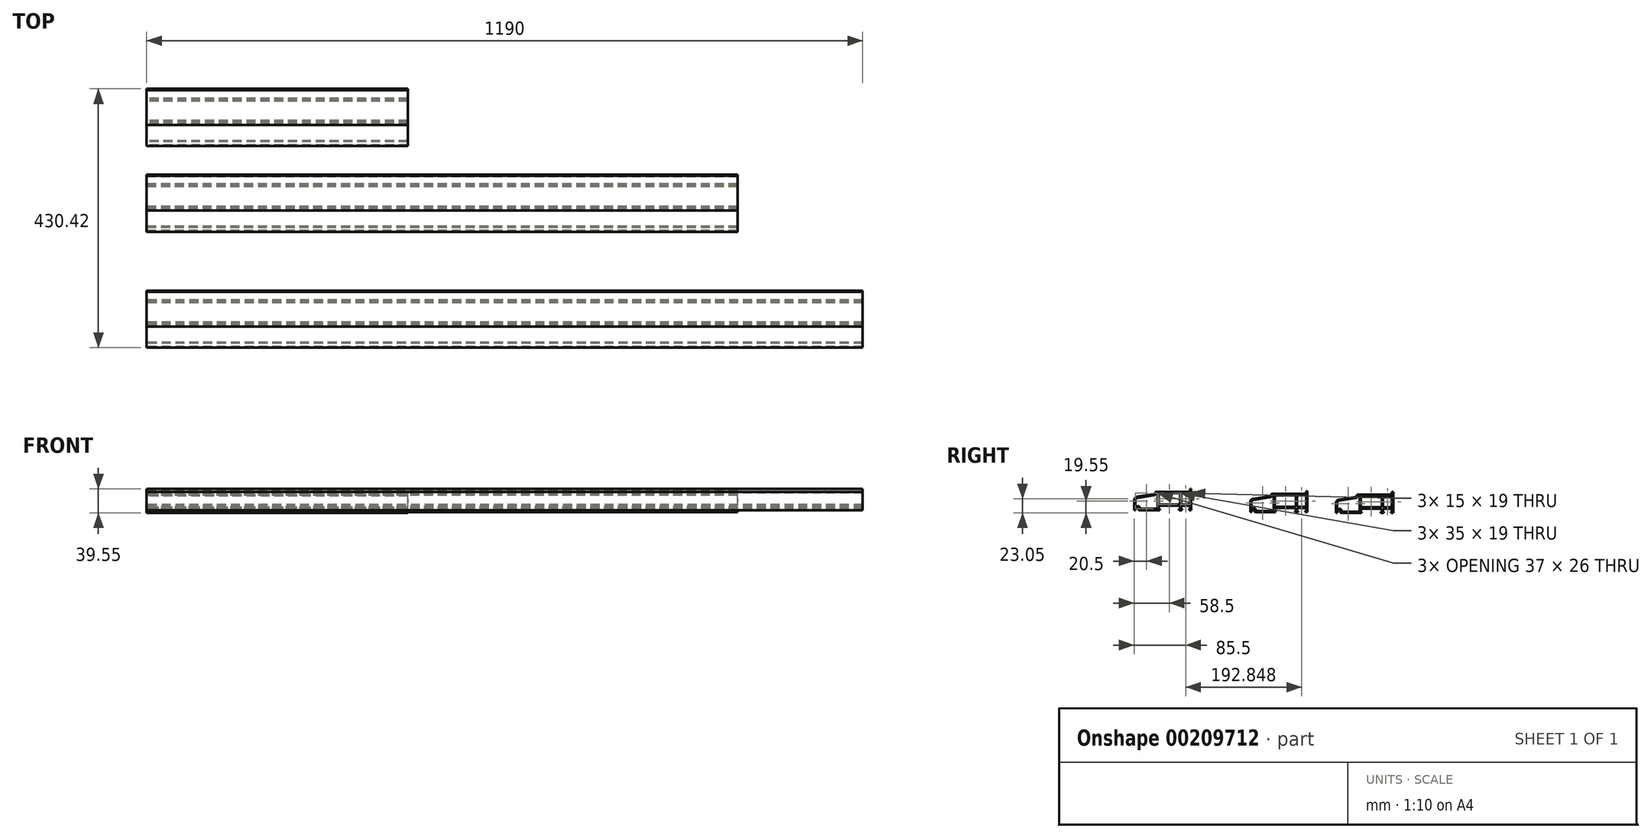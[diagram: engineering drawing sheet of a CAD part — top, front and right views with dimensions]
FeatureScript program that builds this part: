
annotation { "Feature Type Name" : "Feature", "Feature Type Description" : "" }
export const myFeature = defineFeature(function(context is Context, id is Id, definition is map)
    precondition{}
    {
        {
            var Q0;
            Q0=qCreatedBy(makeId("Right.planeOp"),FACE);
            var sketch = newSketch(context, id + "F0", { "sketchPlane" : qUnion([Q0])});
            skLineSegment(sketch, "E0.bottom", {"start": v(0, 0) * mm, "end": v(-3.5, 0) * mm});
            skLineSegment(sketch, "E0.top", {"start": v(-2, 30) * mm, "end": v(-60, 30) * mm});
            skLineSegment(sketch, "E0.left", {"start": v(0, 0) * mm, "end": v(0, 35) * mm});
            skLineSegment(sketch, "E0.right", {"start": v(-95, 0) * mm, "end": v(-95, 16) * mm});
            skArc(sketch, "E1", {"start": v(-89.6, 22.28) * mm, "mid": v(-93.47, 20.14) * mm, "end": v(-95, 16) * mm});
            skLineSegment(sketch, "E2", {"start": v(-89.6, 22.28) * mm, "end": v(-62.97, 26.33) * mm});
            skArc(sketch, "E3", {"start": v(-62.97, 26.33) * mm, "mid": v(-60.77, 27.59) * mm, "end": v(-60, 30) * mm});
            skLineSegment(sketch, "E4.0", {"start": v(-2, 2) * mm, "end": v(-2, 7) * mm});
            skArc(sketch, "E4.1", {"start": v(-62.67, 24.35) * mm, "mid": v(-59.97, 25.56) * mm, "end": v(-58.3, 28) * mm});
            skLineSegment(sketch, "E4.2", {"start": v(-89.3, 20.3) * mm, "end": v(-62.67, 24.35) * mm});
            skLineSegment(sketch, "E4.3", {"start": v(-2, 28) * mm, "end": v(-17, 28) * mm});
            skLineSegment(sketch, "E4.4", {"start": v(-93, 0) * mm, "end": v(-93, 4) * mm});
            skLineSegment(sketch, "E4.5", {"start": v(-2, 2) * mm, "end": v(-3.5, 2) * mm});
            skArc(sketch, "E5.0", {"start": v(-89.3, 20.3) * mm, "mid": v(-91.95, 18.83) * mm, "end": v(-93, 16) * mm});
            skLineSegment(sketch, "E6", {"start": v(-2, 35) * mm, "end": v(0, 35) * mm});
            skLineSegment(sketch, "E7.trimOffspring", {"start": v(-2, 30) * mm, "end": v(-2, 35) * mm});
            skLineSegment(sketch, "E8.0", {"start": v(-17, 2) * mm, "end": v(-17, 7) * mm});
            skLineSegment(sketch, "E9.0", {"start": v(-19, 2) * mm, "end": v(-19, 7) * mm});
            skLineSegment(sketch, "E10.0", {"start": v(-54, 2) * mm, "end": v(-54, 7) * mm});
            skLineSegment(sketch, "E11.0", {"start": v(-56, 2) * mm, "end": v(-56, 28) * mm});
            skLineSegment(sketch, "E12.trimOffspring", {"start": v(-19, 28) * mm, "end": v(-54, 28) * mm});
            skLineSegment(sketch, "E13.trimOffspring", {"start": v(-19, 2) * mm, "end": v(-20.5, 2) * mm});
            skLineSegment(sketch, "E14.trimOffspring", {"start": v(-56, 28) * mm, "end": v(-58.3, 28) * mm});
            skLineSegment(sketch, "E15.trimOffspring", {"start": v(-56, 2) * mm, "end": v(-86, 2) * mm});
            skLineSegment(sketch, "E16.0", {"start": v(-2, 9) * mm, "end": v(-17, 9) * mm});
            skLineSegment(sketch, "E17.0", {"start": v(-2, 7) * mm, "end": v(-17, 7) * mm});
            skLineSegment(sketch, "E18", {"start": v(-52.5, 2) * mm, "end": v(-52.5, 0) * mm});
            skLineSegment(sketch, "E19.trimOffspring", {"start": v(-54, 9) * mm, "end": v(-54, 28) * mm});
            skLineSegment(sketch, "E20", {"start": v(-20.5, 2) * mm, "end": v(-20.5, 0) * mm});
            skLineSegment(sketch, "E21", {"start": v(-15.5, 2) * mm, "end": v(-15.5, 0) * mm});
            skLineSegment(sketch, "E22", {"start": v(-3.5, 2) * mm, "end": v(-3.5, 0) * mm});
            skPoint(sketch, "E23.orphan", {"position": v(-3.5, -2.3) * mm});
            skLineSegment(sketch, "E24.trimOffspring", {"start": v(-15.5, 0) * mm, "end": v(-20.5, 0) * mm});
            skLineSegment(sketch, "E25.trimOffspring", {"start": v(-15.5, 2) * mm, "end": v(-17, 2) * mm});
            skPoint(sketch, "E26.orphan", {"position": v(-15.5, -2.3) * mm});
            skLineSegment(sketch, "E27.trimOffspring", {"start": v(-2, 9) * mm, "end": v(-2, 28) * mm});
            skLineSegment(sketch, "E28.trimOffspring", {"start": v(-17, 9) * mm, "end": v(-17, 28) * mm});
            skLineSegment(sketch, "E29.trimOffspring", {"start": v(-19, 9) * mm, "end": v(-54, 9) * mm});
            skLineSegment(sketch, "E30.trimOffspring", {"start": v(-19, 7) * mm, "end": v(-54, 7) * mm});
            skLineSegment(sketch, "E31.trimOffspring", {"start": v(-19, 9) * mm, "end": v(-19, 28) * mm});
            skPoint(sketch, "E32.orphan", {"position": v(-20.5, -2.3) * mm});
            skLineSegment(sketch, "E33.trimOffspring", {"start": v(-52.5, 2) * mm, "end": v(-54, 2) * mm});
            skLineSegment(sketch, "E34.trimOffspring", {"start": v(-52.5, 0) * mm, "end": v(-86.5, 0) * mm});
            skLineSegment(sketch, "E35", {"start": v(-93, 4) * mm, "end": v(-88.56, 4.57) * mm});
            skLineSegment(sketch, "E36", {"start": v(-88, 4.07) * mm, "end": v(-88, 1.5) * mm});
            skPoint(sketch, "E37.visualSharp", {"position": v(-88, 4.64) * mm});
            skArc(sketch, "E37.filletArc", {"start": v(-88, 4.07) * mm, "mid": v(-88.17, 4.45) * mm, "end": v(-88.56, 4.57) * mm});
            skArc(sketch, "E38.filletArc", {"start": v(-88, 1.5) * mm, "mid": v(-87.56, 0.44) * mm, "end": v(-86.5, 0) * mm});
            skLineSegment(sketch, "E39.0", {"start": v(-86, 4.07) * mm, "end": v(-86, 2) * mm});
            skArc(sketch, "E39.1", {"start": v(-86, 4.07) * mm, "mid": v(-86.85, 5.95) * mm, "end": v(-88.82, 6.55) * mm});
            skLineSegment(sketch, "E39.2", {"start": v(-93, 6.02) * mm, "end": v(-88.82, 6.55) * mm});
            skPoint(sketch, "E40.trimOffspring.end.orphan", {"position": v(-93, 2) * mm});
            skLineSegment(sketch, "E41.trimOffspring", {"start": v(-93, 6.02) * mm, "end": v(-93, 16) * mm});
            skLineSegment(sketch, "E42", {"start": v(-95, 0) * mm, "end": v(-93, 0) * mm});
            skSolve(sketch);
        }
        {
            var Q0;
            Q0 = qSketchRegion(id + "F0", true);
            extrude(context, id + "F1", {"entities" : qUnion([Q0]), "depth" : 1190 * mm, "offsetDistance" : 25 * mm});
        }
        {
            var Q0;
            Q0=qCreatedBy(makeId("Right.planeOp"),FACE);
            var sketch = newSketch(context, id + "F2", { "sketchPlane" : qUnion([Q0])});
            skLineSegment(sketch, "E43.bottom", {"start": v(192.85, -3.3) * mm, "end": v(189.35, -3.3) * mm});
            skLineSegment(sketch, "E43.top", {"start": v(190.85, 26.7) * mm, "end": v(132.85, 26.7) * mm});
            skLineSegment(sketch, "E43.left", {"start": v(192.85, -3.3) * mm, "end": v(192.85, 31.7) * mm});
            skLineSegment(sketch, "E43.right", {"start": v(97.85, -3.3) * mm, "end": v(97.85, 12.7) * mm});
            skArc(sketch, "E44", {"start": v(103.24, 18.98) * mm, "mid": v(99.38, 16.84) * mm, "end": v(97.85, 12.7) * mm});
            skLineSegment(sketch, "E45", {"start": v(103.24, 18.98) * mm, "end": v(129.87, 23.03) * mm});
            skArc(sketch, "E46", {"start": v(129.87, 23.03) * mm, "mid": v(132.07, 24.3) * mm, "end": v(132.85, 26.7) * mm});
            skLineSegment(sketch, "E47.0", {"start": v(190.85, -1.3) * mm, "end": v(190.85, 3.7) * mm});
            skArc(sketch, "E47.1", {"start": v(130.18, 21.05) * mm, "mid": v(132.87, 22.27) * mm, "end": v(134.55, 24.7) * mm});
            skLineSegment(sketch, "E47.2", {"start": v(103.54, 17) * mm, "end": v(130.18, 21.05) * mm});
            skLineSegment(sketch, "E47.3", {"start": v(190.85, 24.7) * mm, "end": v(175.85, 24.7) * mm});
            skLineSegment(sketch, "E47.4", {"start": v(99.85, -3.3) * mm, "end": v(99.85, 0.7) * mm});
            skLineSegment(sketch, "E47.5", {"start": v(190.85, -1.3) * mm, "end": v(189.35, -1.3) * mm});
            skArc(sketch, "E48.0", {"start": v(103.54, 17) * mm, "mid": v(100.9, 15.54) * mm, "end": v(99.85, 12.7) * mm});
            skLineSegment(sketch, "E49", {"start": v(190.85, 31.7) * mm, "end": v(192.85, 31.7) * mm});
            skLineSegment(sketch, "E50.trimOffspring", {"start": v(190.85, 26.7) * mm, "end": v(190.85, 31.7) * mm});
            skLineSegment(sketch, "E51.0", {"start": v(175.85, -1.3) * mm, "end": v(175.85, 3.7) * mm});
            skLineSegment(sketch, "E52.0", {"start": v(173.85, -1.3) * mm, "end": v(173.85, 3.7) * mm});
            skLineSegment(sketch, "E53.0", {"start": v(138.85, -1.3) * mm, "end": v(138.85, 3.7) * mm});
            skLineSegment(sketch, "E54.0", {"start": v(136.85, -1.3) * mm, "end": v(136.85, 24.7) * mm});
            skLineSegment(sketch, "E55.trimOffspring", {"start": v(173.85, 24.7) * mm, "end": v(138.85, 24.7) * mm});
            skLineSegment(sketch, "E56.trimOffspring", {"start": v(173.85, -1.3) * mm, "end": v(172.35, -1.3) * mm});
            skLineSegment(sketch, "E57.trimOffspring", {"start": v(136.85, 24.7) * mm, "end": v(134.55, 24.7) * mm});
            skLineSegment(sketch, "E58.trimOffspring", {"start": v(136.85, -1.3) * mm, "end": v(106.85, -1.3) * mm});
            skLineSegment(sketch, "E59.0", {"start": v(190.85, 5.7) * mm, "end": v(175.85, 5.7) * mm});
            skLineSegment(sketch, "E60.0", {"start": v(190.85, 3.7) * mm, "end": v(175.85, 3.7) * mm});
            skLineSegment(sketch, "E61", {"start": v(140.35, -1.3) * mm, "end": v(140.35, -3.3) * mm});
            skLineSegment(sketch, "E62.trimOffspring", {"start": v(138.85, 5.7) * mm, "end": v(138.85, 24.7) * mm});
            skLineSegment(sketch, "E63", {"start": v(172.35, -1.3) * mm, "end": v(172.35, -3.3) * mm});
            skLineSegment(sketch, "E64", {"start": v(177.35, -1.3) * mm, "end": v(177.35, -3.3) * mm});
            skLineSegment(sketch, "E65", {"start": v(189.35, -1.3) * mm, "end": v(189.35, -3.3) * mm});
            skPoint(sketch, "E66.orphan", {"position": v(189.35, -5.6) * mm});
            skLineSegment(sketch, "E67.trimOffspring", {"start": v(177.35, -3.3) * mm, "end": v(172.35, -3.3) * mm});
            skLineSegment(sketch, "E68.trimOffspring", {"start": v(177.35, -1.3) * mm, "end": v(175.85, -1.3) * mm});
            skPoint(sketch, "E69.orphan", {"position": v(177.35, -5.6) * mm});
            skLineSegment(sketch, "E70.trimOffspring", {"start": v(190.85, 5.7) * mm, "end": v(190.85, 24.7) * mm});
            skLineSegment(sketch, "E71.trimOffspring", {"start": v(175.85, 5.7) * mm, "end": v(175.85, 24.7) * mm});
            skLineSegment(sketch, "E72.trimOffspring", {"start": v(173.85, 5.7) * mm, "end": v(138.85, 5.7) * mm});
            skLineSegment(sketch, "E73.trimOffspring", {"start": v(173.85, 3.7) * mm, "end": v(138.85, 3.7) * mm});
            skLineSegment(sketch, "E74.trimOffspring", {"start": v(173.85, 5.7) * mm, "end": v(173.85, 24.7) * mm});
            skPoint(sketch, "E75.orphan", {"position": v(172.35, -5.6) * mm});
            skLineSegment(sketch, "E76.trimOffspring", {"start": v(140.35, -1.3) * mm, "end": v(138.85, -1.3) * mm});
            skLineSegment(sketch, "E77.trimOffspring", {"start": v(140.35, -3.3) * mm, "end": v(106.35, -3.3) * mm});
            skLineSegment(sketch, "E78", {"start": v(99.85, 0.7) * mm, "end": v(104.28, 1.27) * mm});
            skLineSegment(sketch, "E79", {"start": v(104.85, 0.77) * mm, "end": v(104.85, -1.8) * mm});
            skPoint(sketch, "E80.visualSharp", {"position": v(104.85, 1.34) * mm});
            skArc(sketch, "E80.filletArc", {"start": v(104.85, 0.77) * mm, "mid": v(104.68, 1.15) * mm, "end": v(104.28, 1.27) * mm});
            skArc(sketch, "E81.filletArc", {"start": v(104.85, -1.8) * mm, "mid": v(105.29, -2.86) * mm, "end": v(106.35, -3.3) * mm});
            skLineSegment(sketch, "E82.0", {"start": v(106.85, 0.77) * mm, "end": v(106.85, -1.3) * mm});
            skArc(sketch, "E82.1", {"start": v(106.85, 0.77) * mm, "mid": v(106, 2.65) * mm, "end": v(104.03, 3.25) * mm});
            skLineSegment(sketch, "E82.2", {"start": v(99.85, 2.72) * mm, "end": v(104.03, 3.25) * mm});
            skPoint(sketch, "E83.trimOffspring.end.orphan", {"position": v(99.85, -1.3) * mm});
            skLineSegment(sketch, "E84.trimOffspring", {"start": v(99.85, 2.72) * mm, "end": v(99.85, 12.7) * mm});
            skLineSegment(sketch, "E85", {"start": v(97.85, -3.3) * mm, "end": v(99.85, -3.3) * mm});
            skSolve(sketch);
        }
        {
            var Q0;
            Q0 = qSketchRegion(id + "F2", true);
            extrude(context, id + "F3", {"entities" : qUnion([Q0]), "depth" : 982 * mm, "offsetDistance" : 25 * mm});
        }
        {
            var Q0;
            Q0=qCreatedBy(makeId("Right.planeOp"),FACE);
            var sketch = newSketch(context, id + "F4", { "sketchPlane" : qUnion([Q0])});
            skLineSegment(sketch, "E86.bottom", {"start": v(335.42, -4.55) * mm, "end": v(331.92, -4.55) * mm});
            skLineSegment(sketch, "E86.top", {"start": v(333.42, 25.45) * mm, "end": v(275.42, 25.45) * mm});
            skLineSegment(sketch, "E86.left", {"start": v(335.42, -4.55) * mm, "end": v(335.42, 30.45) * mm});
            skLineSegment(sketch, "E86.right", {"start": v(240.42, -4.55) * mm, "end": v(240.42, 11.45) * mm});
            skArc(sketch, "E87", {"start": v(245.82, 17.72) * mm, "mid": v(241.96, 15.59) * mm, "end": v(240.42, 11.45) * mm});
            skLineSegment(sketch, "E88", {"start": v(245.82, 17.72) * mm, "end": v(272.45, 21.77) * mm});
            skArc(sketch, "E89", {"start": v(272.45, 21.77) * mm, "mid": v(274.65, 23.03) * mm, "end": v(275.42, 25.45) * mm});
            skLineSegment(sketch, "E90.0", {"start": v(333.42, -2.55) * mm, "end": v(333.42, 2.45) * mm});
            skArc(sketch, "E90.1", {"start": v(272.75, 19.8) * mm, "mid": v(275.45, 21.01) * mm, "end": v(277.13, 23.45) * mm});
            skLineSegment(sketch, "E90.2", {"start": v(246.12, 15.75) * mm, "end": v(272.75, 19.8) * mm});
            skLineSegment(sketch, "E90.3", {"start": v(333.42, 23.45) * mm, "end": v(318.42, 23.45) * mm});
            skLineSegment(sketch, "E90.4", {"start": v(242.42, -4.55) * mm, "end": v(242.42, -0.55) * mm});
            skLineSegment(sketch, "E90.5", {"start": v(333.42, -2.55) * mm, "end": v(331.92, -2.55) * mm});
            skArc(sketch, "E91.0", {"start": v(246.12, 15.75) * mm, "mid": v(243.47, 14.28) * mm, "end": v(242.42, 11.45) * mm});
            skLineSegment(sketch, "E92", {"start": v(333.42, 30.45) * mm, "end": v(335.42, 30.45) * mm});
            skLineSegment(sketch, "E93.trimOffspring", {"start": v(333.42, 25.45) * mm, "end": v(333.42, 30.45) * mm});
            skLineSegment(sketch, "E94.0", {"start": v(318.42, -2.55) * mm, "end": v(318.42, 2.45) * mm});
            skLineSegment(sketch, "E95.0", {"start": v(316.42, -2.55) * mm, "end": v(316.42, 2.45) * mm});
            skLineSegment(sketch, "E96.0", {"start": v(281.42, -2.55) * mm, "end": v(281.42, 2.45) * mm});
            skLineSegment(sketch, "E97.0", {"start": v(279.42, -2.55) * mm, "end": v(279.42, 23.45) * mm});
            skLineSegment(sketch, "E98.trimOffspring", {"start": v(316.42, 23.45) * mm, "end": v(281.42, 23.45) * mm});
            skLineSegment(sketch, "E99.trimOffspring", {"start": v(316.42, -2.55) * mm, "end": v(314.92, -2.55) * mm});
            skLineSegment(sketch, "E100.trimOffspring", {"start": v(279.42, 23.45) * mm, "end": v(277.13, 23.45) * mm});
            skLineSegment(sketch, "E101.trimOffspring", {"start": v(279.42, -2.55) * mm, "end": v(249.42, -2.55) * mm});
            skLineSegment(sketch, "E102.0", {"start": v(333.42, 4.45) * mm, "end": v(318.42, 4.45) * mm});
            skLineSegment(sketch, "E103.0", {"start": v(333.42, 2.45) * mm, "end": v(318.42, 2.45) * mm});
            skLineSegment(sketch, "E104", {"start": v(282.92, -2.55) * mm, "end": v(282.92, -4.55) * mm});
            skLineSegment(sketch, "E105.trimOffspring", {"start": v(281.42, 4.45) * mm, "end": v(281.42, 23.45) * mm});
            skLineSegment(sketch, "E106", {"start": v(314.92, -2.55) * mm, "end": v(314.92, -4.55) * mm});
            skLineSegment(sketch, "E107", {"start": v(319.92, -2.55) * mm, "end": v(319.92, -4.55) * mm});
            skLineSegment(sketch, "E108", {"start": v(331.92, -2.55) * mm, "end": v(331.92, -4.55) * mm});
            skPoint(sketch, "E109.orphan", {"position": v(331.92, -6.86) * mm});
            skLineSegment(sketch, "E110.trimOffspring", {"start": v(319.92, -4.55) * mm, "end": v(314.92, -4.55) * mm});
            skLineSegment(sketch, "E111.trimOffspring", {"start": v(319.92, -2.55) * mm, "end": v(318.42, -2.55) * mm});
            skPoint(sketch, "E112.orphan", {"position": v(319.92, -6.86) * mm});
            skLineSegment(sketch, "E113.trimOffspring", {"start": v(333.42, 4.45) * mm, "end": v(333.42, 23.45) * mm});
            skLineSegment(sketch, "E114.trimOffspring", {"start": v(318.42, 4.45) * mm, "end": v(318.42, 23.45) * mm});
            skLineSegment(sketch, "E115.trimOffspring", {"start": v(316.42, 4.45) * mm, "end": v(281.42, 4.45) * mm});
            skLineSegment(sketch, "E116.trimOffspring", {"start": v(316.42, 2.45) * mm, "end": v(281.42, 2.45) * mm});
            skLineSegment(sketch, "E117.trimOffspring", {"start": v(316.42, 4.45) * mm, "end": v(316.42, 23.45) * mm});
            skPoint(sketch, "E118.orphan", {"position": v(314.92, -6.86) * mm});
            skLineSegment(sketch, "E119.trimOffspring", {"start": v(282.92, -2.55) * mm, "end": v(281.42, -2.55) * mm});
            skLineSegment(sketch, "E120.trimOffspring", {"start": v(282.92, -4.55) * mm, "end": v(248.92, -4.55) * mm});
            skLineSegment(sketch, "E121", {"start": v(242.42, -0.55) * mm, "end": v(246.86, 0.01) * mm});
            skLineSegment(sketch, "E122", {"start": v(247.42, -0.48) * mm, "end": v(247.42, -3.05) * mm});
            skPoint(sketch, "E123.visualSharp", {"position": v(247.42, 0.09) * mm});
            skArc(sketch, "E123.filletArc", {"start": v(247.42, -0.48) * mm, "mid": v(247.25, -0.1) * mm, "end": v(246.86, 0.01) * mm});
            skArc(sketch, "E124.filletArc", {"start": v(247.42, -3.05) * mm, "mid": v(247.86, -4.11) * mm, "end": v(248.92, -4.55) * mm});
            skLineSegment(sketch, "E125.0", {"start": v(249.42, -0.48) * mm, "end": v(249.42, -2.55) * mm});
            skArc(sketch, "E125.1", {"start": v(249.42, -0.48) * mm, "mid": v(248.57, 1.4) * mm, "end": v(246.6, 2) * mm});
            skLineSegment(sketch, "E125.2", {"start": v(242.42, 1.46) * mm, "end": v(246.6, 2) * mm});
            skPoint(sketch, "E126.trimOffspring.end.orphan", {"position": v(242.42, -2.55) * mm});
            skLineSegment(sketch, "E127.trimOffspring", {"start": v(242.42, 1.46) * mm, "end": v(242.42, 11.45) * mm});
            skLineSegment(sketch, "E128", {"start": v(240.42, -4.55) * mm, "end": v(242.42, -4.55) * mm});
            skSolve(sketch);
        }
        {
            var Q0;
            Q0 = qSketchRegion(id + "F4", true);
            extrude(context, id + "F5", {"entities" : qUnion([Q0]), "flatOperationType" : FlatOperationType.REMOVE, "depth" : 434 * mm, "offsetDistance" : 25 * mm, "domain" : OperationDomain.MODEL});
        }
    });
